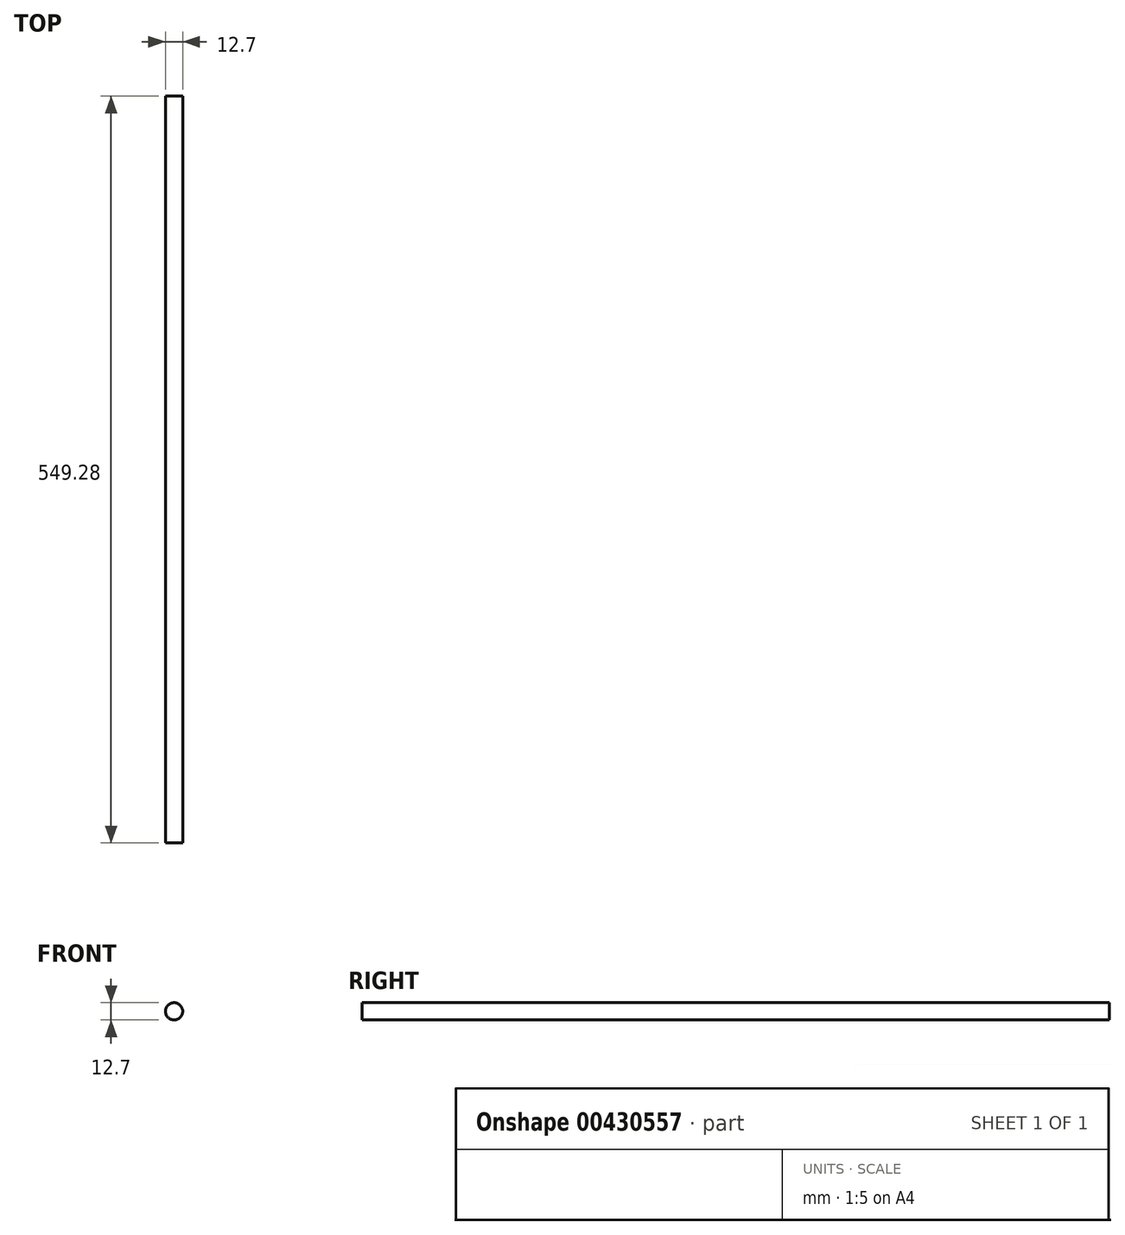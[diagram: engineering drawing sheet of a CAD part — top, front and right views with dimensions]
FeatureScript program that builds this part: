
annotation { "Feature Type Name" : "Feature", "Feature Type Description" : "" }
export const myFeature = defineFeature(function(context is Context, id is Id, definition is map)
    precondition{}
    {
        {
            var Q0;
            Q0=qCreatedBy(makeId("Front.planeOp"),FACE);
            var sketch = newSketch(context, id + "F0", { "sketchPlane" : qUnion([Q0])});
            skCircle(sketch, "E0", {"center": v(0, 0) * mm, "radius": 6.35 * mm});
            skSolve(sketch);
        }
        {
            var Q0;
            Q0=makeQuery(id+"F0.imprint","IMPRINT",FACE,{"disambiguationData":[TD([[makeQuery(id+"F0.imprint","IMPRINT",EDGE,{"derivedFrom":sQuery(id+"F0.wireOp",EDGE,"E0")}),1.0]])]});
            extrude(context, id + "F1", {"entities" : qUnion([Q0]), "depth" : 549.27 * mm});
        }
    });
